# Revit family: Haworth_MSeries_Storage_SwingDoor_AP_PRELIMINARY
name_source: partatom
category: Furniture Systems
units: mm (PartAtom-declared; Revit-internal decimal feet)

## family parameters
Always vertical = Yes
Cut with Voids When Loaded = No
OmniClass Number = 23.40.70.14.64.21
OmniClass Title = Systems Furniture
Part Type = Normal
Room Calculation Point = No
Round Connector Dimension = Use Diameter
Shared = No
Work Plane-Based = No

## types (4) — shared parameters
Actual Depth = 450 mm  [stored 1.47638 ft]
Assembly Code = E2020200
Bottom Case Offset = 30 mm  [stored 0.0984252 ft]
Case Thickness = 20 mm  [stored 0.0656168 ft]
Description = Haworth - M Series - Storage - Swing Door
Distance Between Drawer = 2 mm  [stored 0.00656168 ft]
Glide Finish = Haworth _ Polymer _ Black
Lock Finish = Haworth _ Polymer _ Black
Manufacturer = Haworth
Max. Width = 900 mm  [stored 2.95276 ft]
Min. Width = 750 mm  [stored 2.46063 ft]
Model = STMSSXXN
Pull Finish = Haworth _ Paint _ Smooth Plaster
Revision Number = 1
Size = Verify Final Dim. w/ Haworth
Trim Finish = Haworth _ Polymer _ Black
URL = https://www.haworth.com
URL - Product = https://www.haworth.com
Warranty = http://www.haworth.com

## per-type parameters (varying)
| type | Actual Height | Actual Width | Attached 2Hi | Bottom Drawer Height | Drawer Width | Freestanding 2Hi | Freestanding 3Hi | Freestanding 5Hi | Front Recess Pull | Lock Offset Side | Lock Offset Top | Middle Drawer Height | Premise Pull | Pull Premise Height | Pull Tutti Height | Three Drawer | Top Drawer Height | Total Drawer Height | Touch Latch | Tutti Pull | Two Drawer | Width | with Pull |
| 750w 695h | 695 mm  [stored 2.28018 ft] | 750 mm  [stored 2.46063 ft] | Yes | 330 mm | 373 mm  [stored 1.22375 ft] | No | No | No | No | 338 mm  [stored 1.10892 ft] | 50 mm  [stored 0.164042 ft] | 0 mm  [stored 0 ft] | Yes | 650 mm  [stored 2.13255 ft] | 600 mm | No | 333 mm | 665 mm  [stored 2.18176 ft] | No | No | Yes | 750 mm  [stored 2.46063 ft] | Yes |
| 800w 775h | 775 mm  [stored 2.54265 ft] | 800 mm  [stored 2.62467 ft] | No | 370 mm  [stored 1.21391 ft] | 398 mm  [stored 1.30577 ft] | Yes | No | No | No | 363 mm  [stored 1.19094 ft] | 50 mm  [stored 0.164042 ft] | 0 mm  [stored 0 ft] | No | 730 mm  [stored 2.39501 ft] | 700 mm  [stored 2.29659 ft] | No | 370 mm  [stored 1.21391 ft] | 745 mm | No | Yes | Yes | 800 mm  [stored 2.62467 ft] | Yes |
| 900w 1140h | 1140 mm  [stored 3.74016 ft] | 900 mm  [stored 2.95276 ft] | No | 366 mm | 448 mm  [stored 1.46982 ft] | No | Yes | No | Yes | 413 mm  [stored 1.35499 ft] | 500 mm  [stored 1.64042 ft] | 370 mm  [stored 1.21391 ft] | No | 850 mm  [stored 2.78871 ft] | 850 mm  [stored 2.78871 ft] | Yes | 370 mm  [stored 1.21391 ft] | 1110 mm | Yes | No | No | 900 mm  [stored 2.95276 ft] | No |
| 900w 1800h | 1800 mm  [stored 5.90551 ft] | 900 mm  [stored 2.95276 ft] | No | 366 mm | 448 mm  [stored 1.46982 ft] | No | No | Yes | No | 413 mm  [stored 1.35499 ft] | 950 mm  [stored 3.1168 ft] | 370 mm  [stored 1.21391 ft] | Yes | 1000 mm  [stored 3.28084 ft] | 1200 mm | Yes | 370 mm  [stored 1.21391 ft] | 1770 mm  [stored 5.80709 ft] | No | No | No | 900 mm  [stored 2.95276 ft] | Yes |

note: [stored X ft] marks values corroborated as IEEE doubles in the binary element streams (Revit-internal decimal feet)

## geometry (parser evidence)
native form markers: Blend x8, Sweep x29
no freeform markers — native parametric forms only
